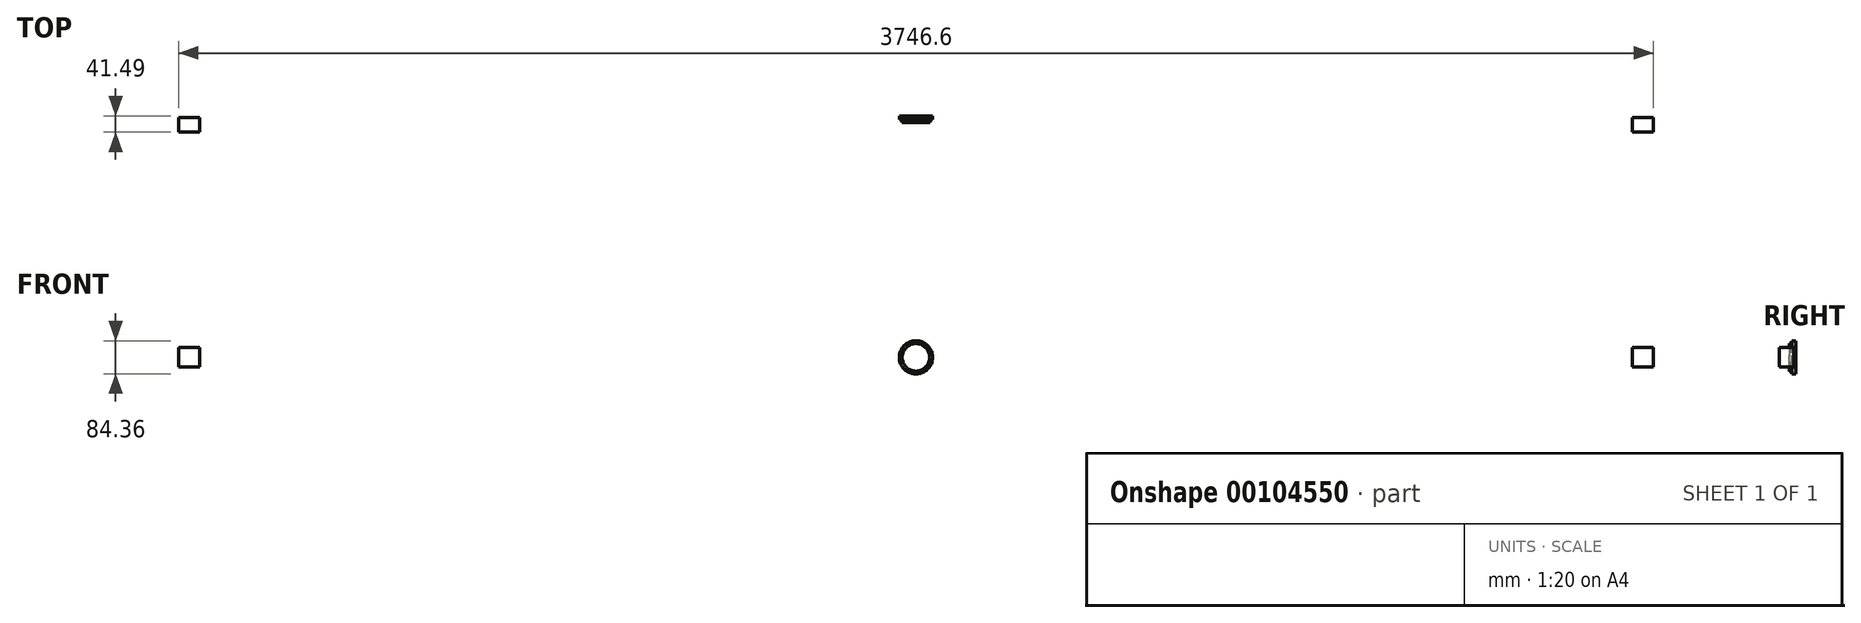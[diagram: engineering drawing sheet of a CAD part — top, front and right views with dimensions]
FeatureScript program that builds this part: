
annotation { "Feature Type Name" : "Feature", "Feature Type Description" : "" }
export const myFeature = defineFeature(function(context is Context, id is Id, definition is map)
    precondition{}
    {
        {
            var Q0;
            Q0=qCreatedBy(makeId("Front.planeOp"),FACE);
            var sketch = newSketch(context, id + "F0", { "sketchPlane" : qUnion([Q0])});
            skCircle(sketch, "E0", {"center": v(0, 0) * mm, "radius": 42.18 * mm});
            skSolve(sketch);
        }
        {
            var Q0;
            Q0 = qSketchRegion(id + "F0", true);
            extrude(context, id + "F1", {"entities" : qUnion([Q0]), "endBound" : BoundingType.SYMMETRIC, "depth" : 9.5 * mm});
        }
        {
            var Q0;
            Q0=makeQuery(id+"F1.opExtrude","CAP_FACE",FACE,{"disambiguationData":[OSD([sQuery(id+"F0.wireOp",EDGE,"E0")])],"isStart":false});
            var sketch = newSketch(context, id + "F2", { "sketchPlane" : qUnion([Q0])});
            skCircle(sketch, "E1", {"center": v(0, 0) * mm, "radius": 35.1 * mm});
            skSolve(sketch);
        }
        {
            var Q0;
            Q0 = qSketchRegion(id + "F2", true);
            extrude(context, id + "F3", {"entities" : qUnion([Q0]), "operationType" : NewBodyOperationType.ADD, "depth" : 6.8 * mm});
        }
        {
            var Q0;
            Q0=qCreatedBy(makeId("Front.planeOp"),FACE);
            var sketch = newSketch(context, id + "F4", { "sketchPlane" : qUnion([Q0])});
            skLineSegment(sketch, "E2.bottom", {"start": v(1873.3, 24.74) * mm, "end": v(1819.62, 24.74) * mm});
            skLineSegment(sketch, "E2.top", {"start": v(1873.3, -24.74) * mm, "end": v(1819.62, -24.74) * mm});
            skLineSegment(sketch, "E2.left", {"start": v(1873.3, 24.74) * mm, "end": v(1873.3, -24.74) * mm});
            skLineSegment(sketch, "E2.right", {"start": v(1819.62, 24.74) * mm, "end": v(1819.62, -24.74) * mm});
            skPoint(sketch, "E2.middle", {"position": v(1846.46, 0) * mm});
            skLineSegment(sketch, "E3.MirrorCS", {"start": v(-1873.3, 24.74) * mm, "end": v(-1873.3, -24.74) * mm});
            skLineSegment(sketch, "E4.MirrorCS", {"start": v(-1873.3, -24.74) * mm, "end": v(-1819.62, -24.74) * mm});
            skLineSegment(sketch, "E5.MirrorCS", {"start": v(-1819.62, 24.74) * mm, "end": v(-1819.62, -24.74) * mm});
            skLineSegment(sketch, "E6.MirrorCS", {"start": v(-1873.3, 24.74) * mm, "end": v(-1819.62, 24.74) * mm});
            skSolve(sketch);
        }
        {
            var Q0;
            Q0 = qSketchRegion(id + "F4", true);
            extrude(context, id + "F5", {"entities" : qUnion([Q0]), "operationType" : NewBodyOperationType.ADD, "depth" : 36.74 * mm});
        }
    });
